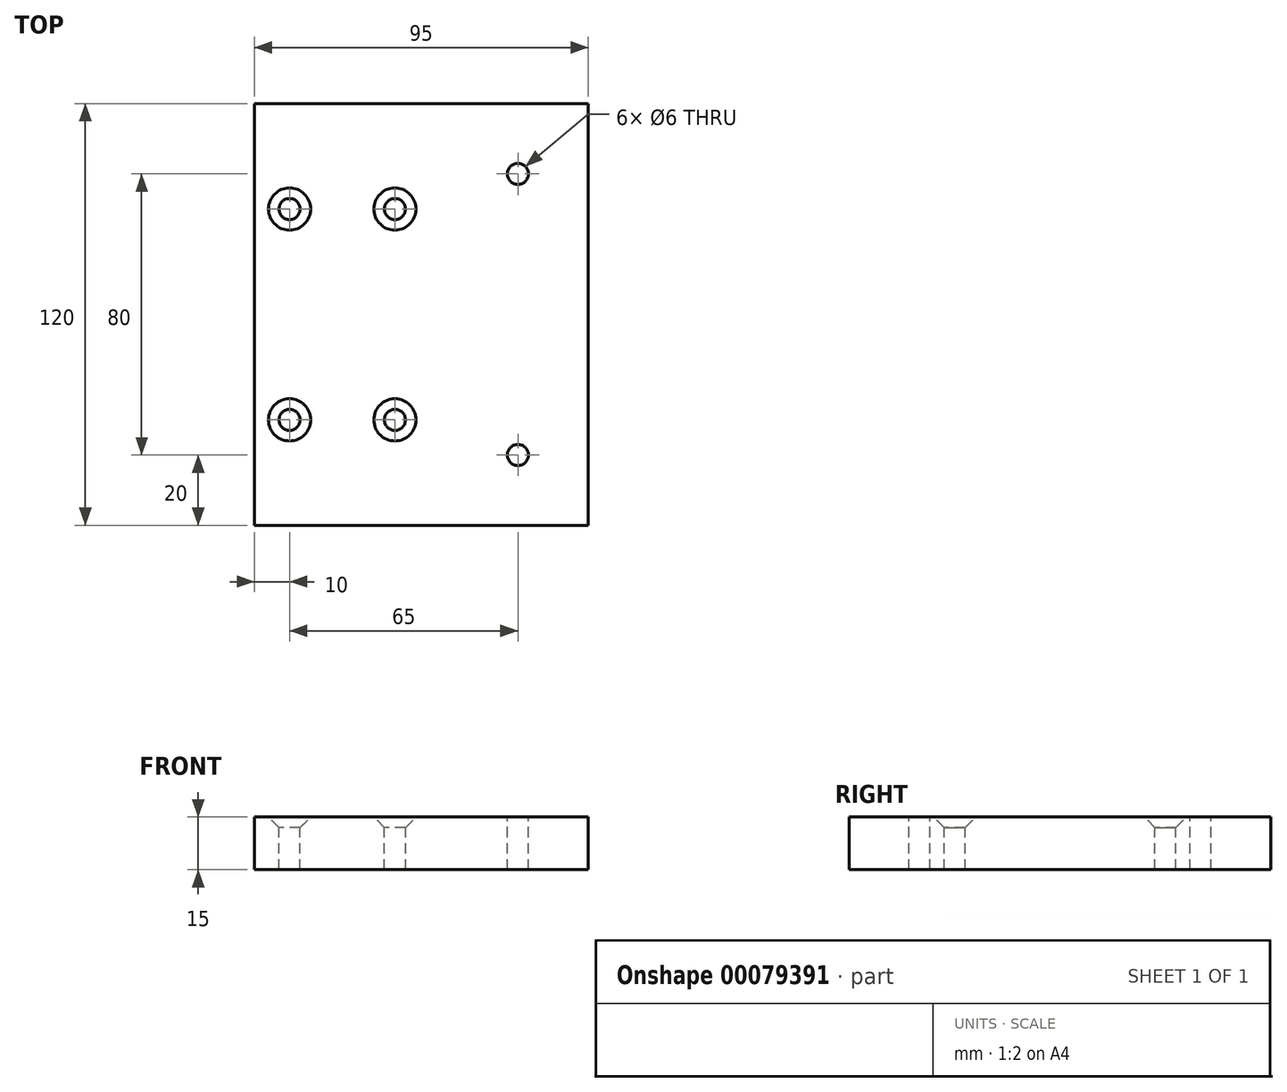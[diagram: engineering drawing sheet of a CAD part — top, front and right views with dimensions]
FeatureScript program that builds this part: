
annotation { "Feature Type Name" : "Feature", "Feature Type Description" : "" }
export const myFeature = defineFeature(function(context is Context, id is Id, definition is map)
    precondition{}
    {
        {
            var Q0;
            Q0=qCreatedBy(makeId("Top.planeOp"),FACE);
            var sketch = newSketch(context, id + "F0", { "sketchPlane" : qUnion([Q0])});
            skLineSegment(sketch, "E0.bottom", {"start": v(-47.5, 60) * mm, "end": v(47.5, 60) * mm});
            skLineSegment(sketch, "E0.top", {"start": v(-47.5, -60) * mm, "end": v(47.5, -60) * mm});
            skLineSegment(sketch, "E0.left", {"start": v(-47.5, 60) * mm, "end": v(-47.5, -60) * mm});
            skLineSegment(sketch, "E0.right", {"start": v(47.5, 60) * mm, "end": v(47.5, -60) * mm});
            skPoint(sketch, "E0.middle", {"position": v(0, 0) * mm});
            skCircle(sketch, "E1", {"center": v(-37.5, 30) * mm, "radius": 3 * mm});
            skCircle(sketch, "E2", {"center": v(-7.5, 30) * mm, "radius": 3 * mm});
            skCircle(sketch, "E3.MirrorC", {"center": v(-7.5, -30) * mm, "radius": 3 * mm});
            skCircle(sketch, "E4.MirrorC", {"center": v(-37.5, -30) * mm, "radius": 3 * mm});
            skCircle(sketch, "E5", {"center": v(27.5, 40) * mm, "radius": 3 * mm});
            skCircle(sketch, "E6.MirrorC", {"center": v(27.5, -40) * mm, "radius": 3 * mm});
            skSolve(sketch);
        }
        {
            var Q0;
            Q0 = qSketchRegion(id + "F0", true);
            var Q1;
            Q1=makeQuery(id+"F0.imprint","IMPRINT",FACE,{"disambiguationData":[TD([[makeQuery(id+"F0.imprint","IMPRINT",EDGE,{"derivedFrom":sQuery(id+"F0.wireOp",EDGE,"E1")}),1.0]])]});
            var Q2;
            Q2=makeQuery(id+"F0.imprint","IMPRINT",FACE,{"disambiguationData":[TD([[makeQuery(id+"F0.imprint","IMPRINT",EDGE,{"derivedFrom":sQuery(id+"F0.wireOp",EDGE,"E4.MirrorC")}),-1.0]])]});
            var Q3;
            Q3=makeQuery(id+"F0.imprint","IMPRINT",FACE,{"disambiguationData":[TD([[makeQuery(id+"F0.imprint","IMPRINT",EDGE,{"derivedFrom":sQuery(id+"F0.wireOp",EDGE,"E3.MirrorC")}),-1.0]])]});
            var Q4;
            Q4=makeQuery(id+"F0.imprint","IMPRINT",FACE,{"disambiguationData":[TD([[makeQuery(id+"F0.imprint","IMPRINT",EDGE,{"derivedFrom":sQuery(id+"F0.wireOp",EDGE,"E6.MirrorC")}),-1.0]])]});
            var Q5;
            Q5=makeQuery(id+"F0.imprint","IMPRINT",FACE,{"disambiguationData":[TD([[makeQuery(id+"F0.imprint","IMPRINT",EDGE,{"derivedFrom":sQuery(id+"F0.wireOp",EDGE,"E2")}),1.0]])]});
            var Q6;
            Q6=makeQuery(id+"F0.imprint","IMPRINT",FACE,{"disambiguationData":[TD([[makeQuery(id+"F0.imprint","IMPRINT",EDGE,{"derivedFrom":sQuery(id+"F0.wireOp",EDGE,"E5")}),1.0]])]});
            extrude(context, id + "F1", {"entities" : qUnion([Q0, Q1, Q2, Q3, Q4, Q5, Q6]), "oppositeDirection" : true, "depth" : 15 * mm});
        }
        {
            var Q0;
            Q0=sQuery(id+"F0.wireOp",VERTEX,"E1.center");
            var Q1;
            Q1=sQuery(id+"F0.wireOp",VERTEX,"E2.center");
            var Q2;
            Q2=sQuery(id+"F0.wireOp",VERTEX,"E4.MirrorC.center");
            var Q3;
            Q3=sQuery(id+"F0.wireOp",VERTEX,"E3.MirrorC.center");
            var Q4;
            Q4=makeQuery(id+"F1.opExtrude","SWEPT_BODY",BODY,{"disambiguationData":[OSD([sQuery(id+"F0.wireOp",EDGE,"E0.bottom"),sQuery(id+"F0.wireOp",EDGE,"E0.top"),sQuery(id+"F0.wireOp",EDGE,"E0.left"),sQuery(id+"F0.wireOp",EDGE,"E0.right")])]});
            hole(context, id + "F2", {"style" : HoleStyle.C_SINK, "endStyle" : HoleEndStyle.THROUGH, "holeDiameter" : 6 * mm, "cSinkDiameter" : 12 * mm, "cSinkAngle" : 90 * degree, "locations" : qUnion([Q0, Q1, Q2, Q3]), "scope" : qUnion([Q4]), "isTappedThrough" : true});
        }
        {
            var Q0;
            Q0=sQuery(id+"F0.wireOp",VERTEX,"E5.center");
            var Q1;
            Q1=sQuery(id+"F0.wireOp",VERTEX,"E6.MirrorC.center");
            var Q2;
            Q2=makeQuery(id+"F1.opExtrude","SWEPT_BODY",BODY,{"disambiguationData":[OSD([sQuery(id+"F0.wireOp",EDGE,"E0.bottom"),sQuery(id+"F0.wireOp",EDGE,"E0.top"),sQuery(id+"F0.wireOp",EDGE,"E0.left"),sQuery(id+"F0.wireOp",EDGE,"E0.right")])]});
            hole(context, id + "F3", {"style" : HoleStyle.SIMPLE, "endStyle" : HoleEndStyle.THROUGH, "holeDiameter" : 6 * mm, "locations" : qUnion([Q0, Q1]), "scope" : qUnion([Q2]), "isTappedThrough" : true});
        }
    });
